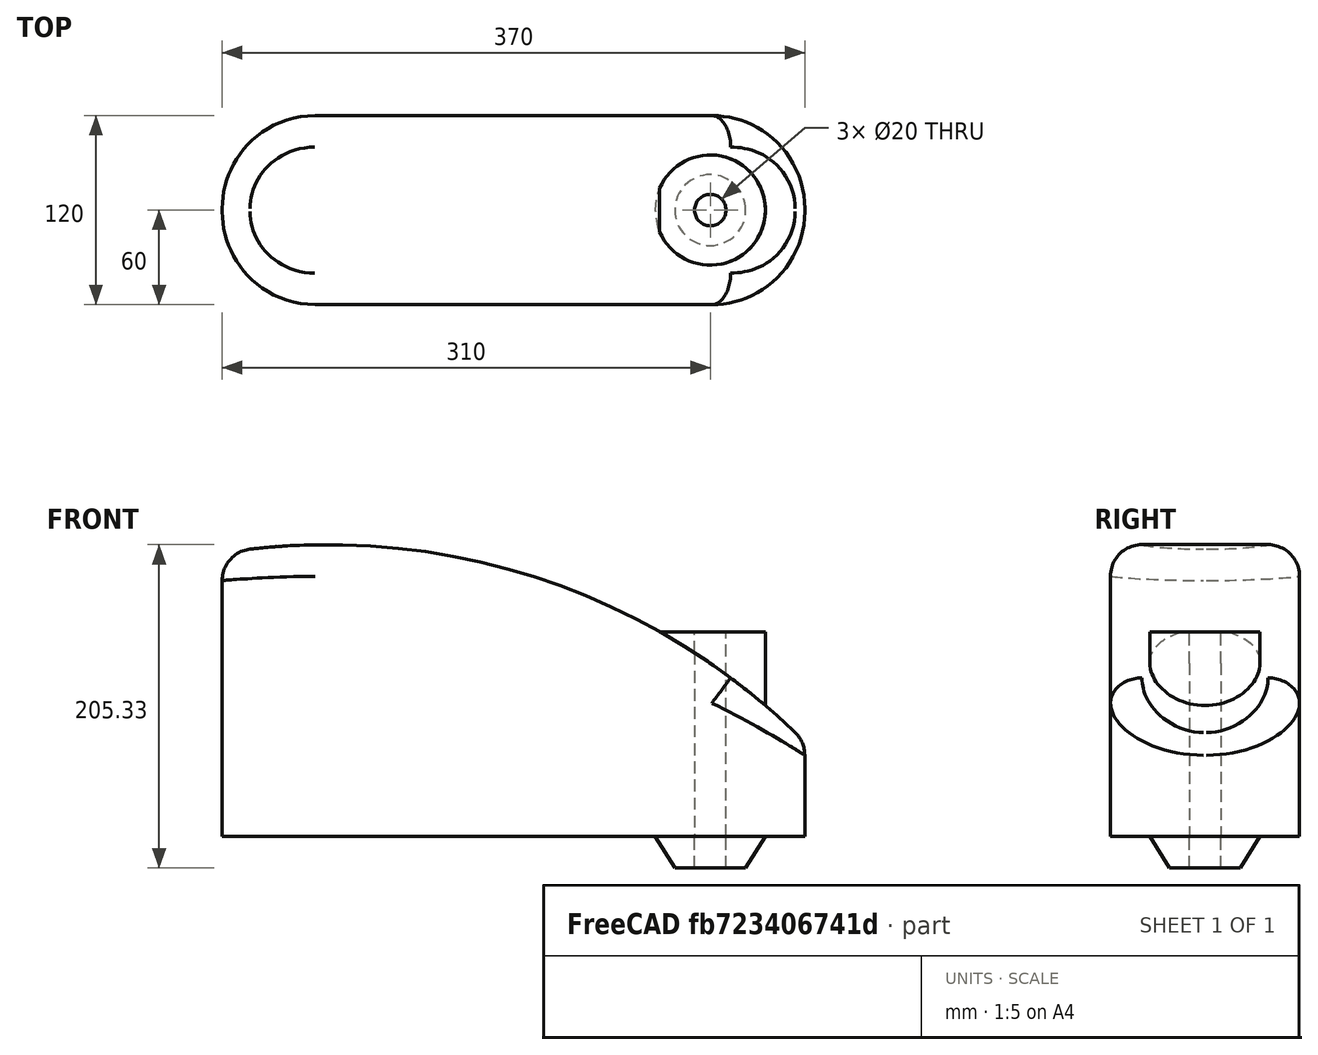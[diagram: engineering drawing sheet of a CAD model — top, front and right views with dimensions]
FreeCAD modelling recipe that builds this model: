
FCSTD DOCUMENT  (FreeCAD 0.20R29410 (Git))
Label: lk2
License: All rights reserved
LicenseURL: http://en.wikipedia.org/wiki/All_rights_reserved
objects: PartDesign::Fillet×5, Sketcher::SketchObject×3, PartDesign::Pad×1, PartDesign::Pocket×1, PartDesign::Revolution×1, PartDesign::Body×1, Mesh::Feature×1
note: 20 computed .brp shape members not serialized (recipe doc carries the construction recipe); baked Part::Feature solids carry a one-line shape summary decoded from their .brp

FEATURE [Sketcher::SketchObject] Sketch
  FullyConstrained = false
  MapMode = 5
  Placement = pos=(0,0,0) rot=(1,0,0;1.5708rad)
  Support = -> [XZ_Plane]
  sketch-geometry (5):
    g0: LineSegment StartX=-60 StartY=0 StartZ=0 EndX=310 EndY=0 EndZ=0
    g1: LineSegment StartX=310 StartY=0 StartZ=0 EndX=310 EndY=60 EndZ=0
    g2: LineSegment StartX=-60 StartY=0 StartZ=0 EndX=-60 EndY=180 EndZ=0
    g3: ArcOfCircle CenterX=7.34562 CenterY=-242.768 CenterZ=0 NormalX=0 NormalY=0 NormalZ=1 AngleXU=0 Radius=428.098 StartAngle=0.785585 EndAngle=1.72877
    g4: GeomPoint X=250 Y=0 Z=0
  constraints (14):
    c: PointOnObject(g0,g-1)
    c: PointOnObject(g0,g-1)
    c: Coincident(g1,g0)
    c: Vertical(g1)
    c: Coincident(g2,g0)
    c: Vertical(g2)
    c: DistanceX(g0,g-1) = 60
    c: Coincident(g3,g2)
    c: Coincident(g3,g1)
    c: PointOnObject(g4,g0)
    c: DistanceX(g4,g0) = 60
    c: DistanceX(g-1,g4) = 250
    c: DistanceY(g2,g2) = 180
    c: DistanceY(g1,g1) = 60
FEATURE [PartDesign::Pad] Pad
  Direction = (1,1,1)
  Length = 120
  Length2 = 100
  Midplane = true
  Placement = pos=(0,0,0) rot=(1,0,0;1.5708rad)
  Profile = -> Sketch
  Reversed = true
  Type = 0
FEATURE [PartDesign::Fillet] Fillet
  Base = -> Pad [Edge11]
  BaseFeature = -> Pad
  Placement = pos=(0,0,0) rot=(1,0,0;1.5708rad)
  Radius = 59
  SupportTransform = false
  UseAllEdges = false
FEATURE [PartDesign::Fillet] Fillet001
  Base = -> Fillet [Edge7]
  BaseFeature = -> Fillet
  Placement = pos=(0,0,0) rot=(1,0,0;1.5708rad)
  Radius = 59
  SupportTransform = false
  UseAllEdges = false
FEATURE [PartDesign::Fillet] Fillet002
  Base = -> Fillet001 [Edge14]
  BaseFeature = -> Fillet001
  Placement = pos=(0,0,0) rot=(1,0,0;1.5708rad)
  Radius = 59
  SupportTransform = false
  UseAllEdges = false
FEATURE [PartDesign::Fillet] Fillet003
  Base = -> Fillet002 [Edge15]
  BaseFeature = -> Fillet002
  Placement = pos=(0,0,0) rot=(1,0,0;1.5708rad)
  Radius = 59
  SupportTransform = false
  UseAllEdges = false
FEATURE [PartDesign::Fillet] Fillet004
  Base = -> Fillet003 [Face10]
  BaseFeature = -> Fillet003
  Placement = pos=(0,0,0) rot=(1,0,0;1.5708rad)
  Radius = 20
  SupportTransform = false
  UseAllEdges = false
FEATURE [Sketcher::SketchObject] Sketch001
  FullyConstrained = true
  MapMode = 5
  Support = -> [XY_Plane]
  sketch-geometry (1):
    g0: Circle CenterX=250 CenterY=0 CenterZ=0 NormalX=0 NormalY=0 NormalZ=1 AngleXU=0 Radius=10
  constraints (3):
    c: PointOnObject(g0,g-1)
    c: Diameter(g0) = 20
    c: DistanceX(g-1,g0) = 250
FEATURE [PartDesign::Pocket] Pocket
  BaseFeature = -> Fillet004
  Direction = (1,1,1)
  Length = 60
  Length2 = 100
  Placement = pos=(0,0,0) rot=(1,0,0;1.5708rad)
  Profile = -> Sketch001
  Reversed = true
  Type = 1
FEATURE [Sketcher::SketchObject] Sketch002
  FullyConstrained = false
  MapMode = 5
  Placement = pos=(0,0,0) rot=(1,0,0;1.5708rad)
  Support = -> [XZ_Plane]
  sketch-geometry (7):
    g0: LineSegment StartX=250 StartY=-112.488 StartZ=0 EndX=250 EndY=333.985 EndZ=0
    g1: LineSegment StartX=260 StartY=-20 StartZ=0 EndX=260 EndY=130 EndZ=0
    g2: LineSegment StartX=260 StartY=130 StartZ=0 EndX=285 EndY=130 EndZ=0
    g3: LineSegment StartX=285 StartY=130 StartZ=0 EndX=285 EndY=0 EndZ=0
    g4: LineSegment StartX=285 StartY=0 StartZ=0 EndX=272.5 EndY=-20 EndZ=0
    g5: LineSegment StartX=272.5 StartY=-20 StartZ=0 EndX=260 EndY=-20 EndZ=0
    g6: GeomPoint X=272.5 Y=130 Z=0
  constraints (18):
    c: Vertical(g0)
    c: DistanceX(g-1,g0) = 250
    c: Vertical(g1)
    c: Coincident(g2,g1)
    c: Horizontal(g2)
    c: Coincident(g3,g2)
    c: PointOnObject(g3,g-1)
    c: Vertical(g3)
    c: Coincident(g5,g4)
    c: Coincident(g5,g1)
    c: Horizontal(g5)
    c: DistanceX(g0,g1) = 10
    c: DistanceY(g1,g4) = 20
    c: DistanceX(g2,g2) = 25
    c: DistanceY(g-1,g1) = 130
    c: Coincident(g4,g3)
    c: Symmetric(g2,g1,g6)
    c: Vertical(g4,g6)
FEATURE [PartDesign::Revolution] Revolution
  Angle = 360
  Axis = (0,-9.91e-14,446.472)
  Base = (250,2.5e-14,-112.488)
  BaseFeature = -> Pocket
  Placement = pos=(0,0,0) rot=(1,0,0;1.5708rad)
  Profile = -> Sketch002
  ReferenceAxis = -> Sketch002 [Axis0]
  Reversed = true
FEATURE [PartDesign::Body] Body
  Group = -> [Sketch,Pad,Fillet,Fillet001,Fillet002,Fillet003,Fillet004,Sketch001,Pocket,Sketch002,Revolution]
  Origin = -> Origin
  Tip = -> Revolution
FEATURE [Mesh::Feature] Mesh  label="Revolution (Meshed)"
